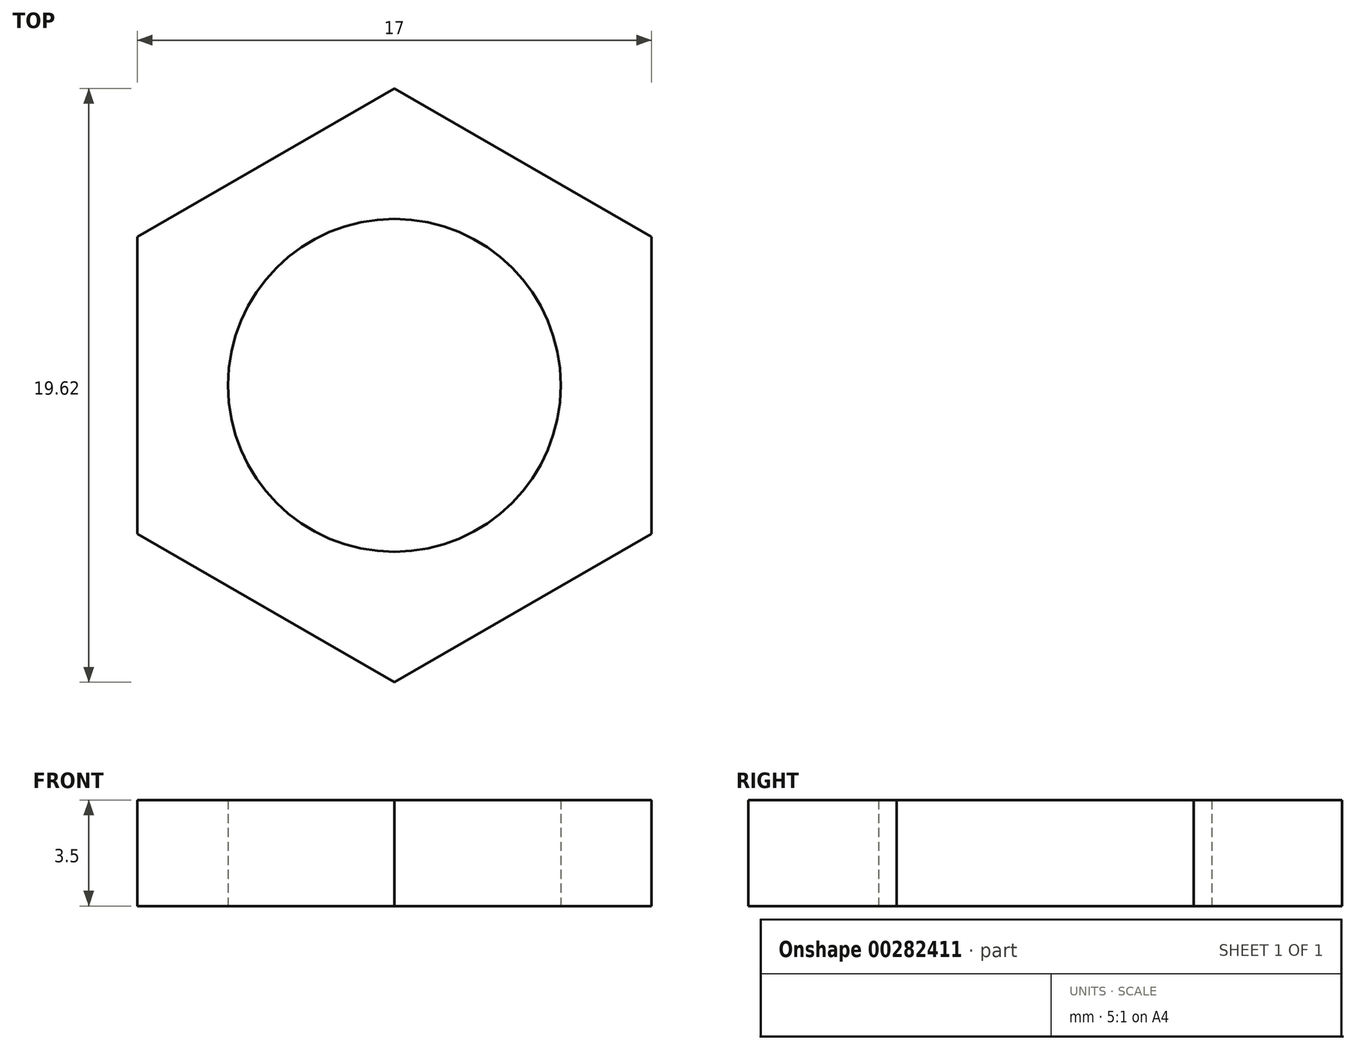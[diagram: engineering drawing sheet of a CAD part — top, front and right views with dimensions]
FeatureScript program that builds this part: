
annotation { "Feature Type Name" : "Feature", "Feature Type Description" : "" }
export const myFeature = defineFeature(function(context is Context, id is Id, definition is map)
    precondition{}
    {
        {
            var Q0;
            Q0=qCreatedBy(makeId("Top.planeOp"),FACE);
            var sketch = newSketch(context, id + "F0", { "sketchPlane" : qUnion([Q0])});
            skCircle(sketch, "E0.cCircle", {"center": v(0, 0) * mm, "radius": 8.5 * mm, "construction": true});
            skLineSegment(sketch, "E0.0", {"start": v(8.5, -4.9) * mm, "end": v(0, -9.81) * mm});
            skLineSegment(sketch, "E0.1", {"start": v(0, -9.81) * mm, "end": v(-8.5, -4.9) * mm});
            skLineSegment(sketch, "E0.2", {"start": v(-8.5, -4.9) * mm, "end": v(-8.5, 4.9) * mm});
            skLineSegment(sketch, "E0.3", {"start": v(-8.5, 4.9) * mm, "end": v(0, 9.81) * mm});
            skLineSegment(sketch, "E0.4", {"start": v(0, 9.81) * mm, "end": v(8.5, 4.9) * mm});
            skLineSegment(sketch, "E0.5", {"start": v(8.5, 4.9) * mm, "end": v(8.5, -4.9) * mm});
            skPoint(sketch, "E0.0.midPoint", {"position": v(4.25, -7.36) * mm});
            skLineSegment(sketch, "E1", {"start": v(0, 0) * mm, "end": v(0, 9.81) * mm, "construction": true});
            skCircle(sketch, "E2", {"center": v(0, 0) * mm, "radius": 5.5 * mm});
            skSolve(sketch);
        }
        {
            var Q0;
            Q0=qSketchRegion(id+"F0",true);
            extrude(context, id + "F1", {"entities" : qUnion([Q0]), "depth" : 3.5 * mm});
        }
    });
